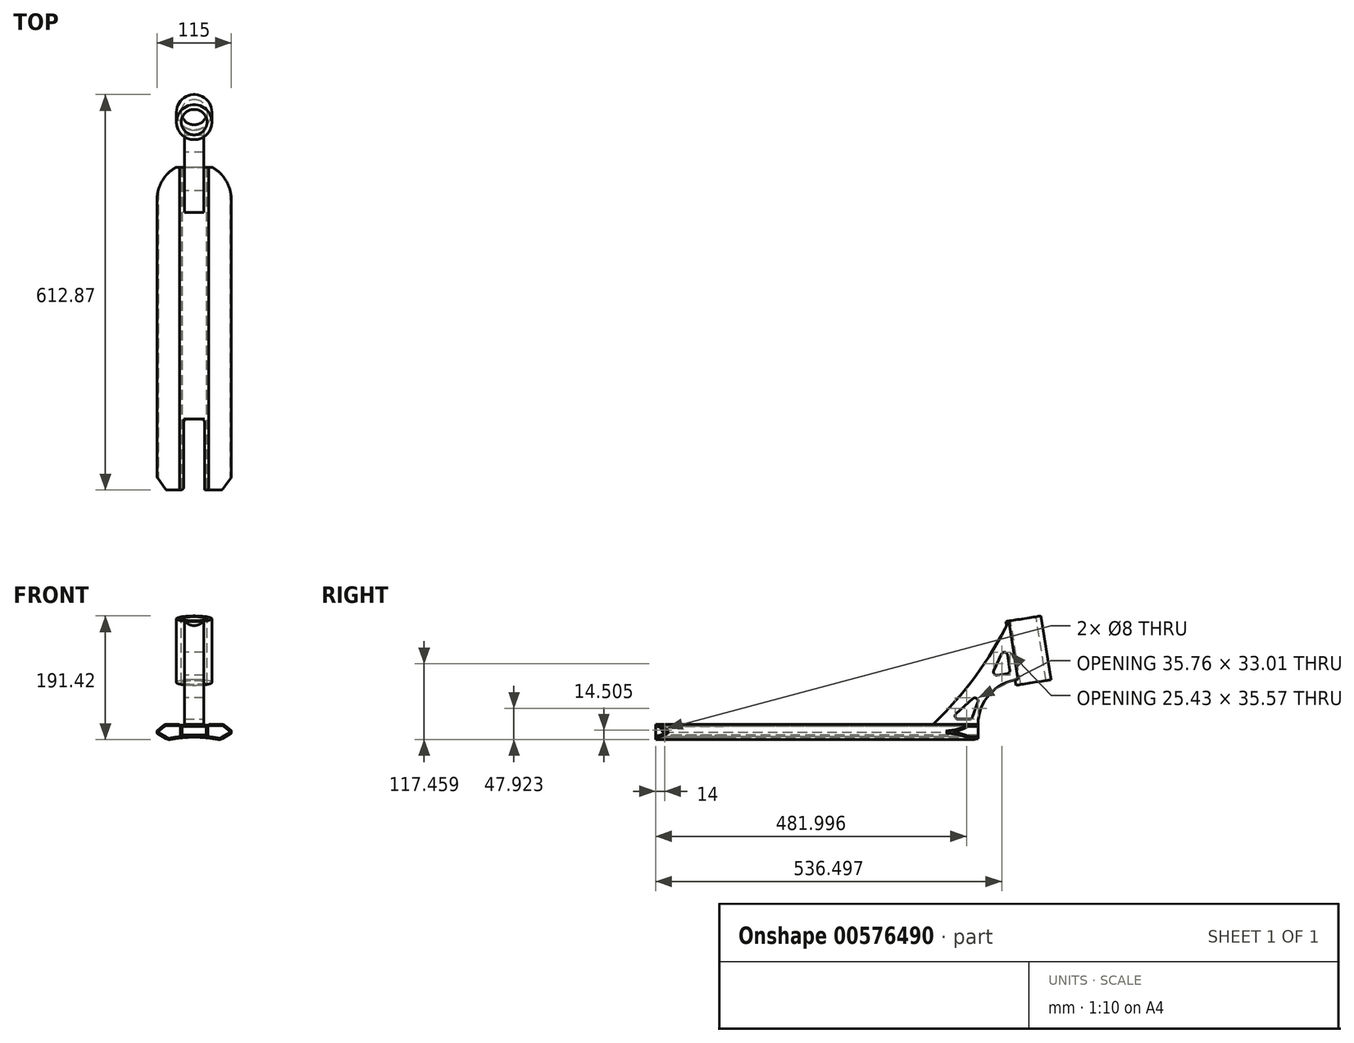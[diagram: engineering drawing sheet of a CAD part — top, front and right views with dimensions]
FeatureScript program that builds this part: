
annotation { "Feature Type Name" : "Feature", "Feature Type Description" : "" }
export const myFeature = defineFeature(function(context is Context, id is Id, definition is map)
    precondition{}
    {
        {
            var Q0;
            Q0=qCreatedBy(makeId("Front.planeOp"),FACE);
            var sketch = newSketch(context, id + "F0", { "sketchPlane" : qUnion([Q0])});
            skLineSegment(sketch, "E0", {"start": v(0, 18.62) * mm, "end": v(22.5, 18.62) * mm});
            skLineSegment(sketch, "E1", {"start": v(22.5, 18.62) * mm, "end": v(22.5, 19.92) * mm});
            skLineSegment(sketch, "E2", {"start": v(22.5, 19.92) * mm, "end": v(45.58, 19.92) * mm});
            skLineSegment(sketch, "E3", {"start": v(45.58, 19.92) * mm, "end": v(57.5, 9.92) * mm});
            skLineSegment(sketch, "E4", {"start": v(57.5, 9.92) * mm, "end": v(57.5, 5.92) * mm});
            skLineSegment(sketch, "E5", {"start": v(57.5, 5.92) * mm, "end": v(40.18, -4.08) * mm});
            skLineSegment(sketch, "E6.MirrorCS", {"start": v(0, 18.62) * mm, "end": v(-22.5, 18.62) * mm});
            skLineSegment(sketch, "E7.MirrorCS", {"start": v(-22.5, 18.62) * mm, "end": v(-22.5, 19.92) * mm});
            skLineSegment(sketch, "E8.MirrorCS", {"start": v(-22.5, 19.92) * mm, "end": v(-45.58, 19.92) * mm});
            skLineSegment(sketch, "E9.MirrorCS", {"start": v(-45.58, 19.92) * mm, "end": v(-57.5, 9.92) * mm});
            skLineSegment(sketch, "E10.MirrorCS", {"start": v(-57.5, 9.92) * mm, "end": v(-57.5, 5.92) * mm});
            skLineSegment(sketch, "E11.MirrorCS", {"start": v(-57.5, 5.92) * mm, "end": v(-40.18, -4.08) * mm});
            skArc(sketch, "E12", {"start": v(40.18, -4.08) * mm, "mid": v(0, 0) * mm, "end": v(-40.18, -4.08) * mm});
            skSolve(sketch);
        }
        {
            var Q0;
            Q0=makeQuery(id+"F0.imprint","IMPRINT",FACE,{"disambiguationData":[TD([[makeQuery(id+"F0.imprint","IMPRINT",EDGE,{"derivedFrom":sQuery(id+"F0.wireOp",EDGE,"E0")}),-1.0]])]});
            extrude(context, id + "F1", {"entities" : qUnion([Q0]), "endBound" : BoundingType.SYMMETRIC, "depth" : 500 * mm, "offsetDistance" : 25 * mm});
        }
        {
            var Q0;
            Q0=qCreatedBy(makeId("Front.planeOp"),FACE);
            var sketch = newSketch(context, id + "F2", { "sketchPlane" : qUnion([Q0])});
            skLineSegment(sketch, "E13.bottom", {"start": v(-19, 16.62) * mm, "end": v(19, 16.62) * mm});
            skLineSegment(sketch, "E13.top", {"start": v(-19, 3.62) * mm, "end": v(19, 3.62) * mm});
            skLineSegment(sketch, "E13.left", {"start": v(-19, 16.62) * mm, "end": v(-19, 3.62) * mm});
            skLineSegment(sketch, "E13.right", {"start": v(19, 16.62) * mm, "end": v(19, 3.62) * mm});
            skSolve(sketch);
        }
        {
            var Q0;
            Q0 = qSketchRegion(id + "F2", true);
            extrude(context, id + "F3", {"entities" : qUnion([Q0]), "operationType" : NewBodyOperationType.REMOVE, "endBound" : BoundingType.SYMMETRIC, "oppositeDirection" : true, "depth" : 500 * mm, "offsetDistance" : 25 * mm});
        }
        {
            var Q0;
            Q0=makeQuery(id+"F1.opExtrude","SWEPT_EDGE",EDGE,{"disambiguationData":[OSD([sQuery(id+"F0.wireOp",EDGE,"E7.MirrorCS"),sQuery(id+"F0.wireOp",EDGE,"E8.MirrorCS")])]});
            var Q1;
            Q1=makeQuery(id+"F1.opExtrude","SWEPT_EDGE",EDGE,{"disambiguationData":[OSD([sQuery(id+"F0.wireOp",EDGE,"E1"),sQuery(id+"F0.wireOp",EDGE,"E2")])]});
            fillet(context, id + "F4", {"entities" : qUnion([Q0, Q1]), "radius" : 2 * mm, "tangentPropagation" : true, "allowEdgeOverflow" : false});
        }
        {
            var Q0;
            Q0=makeQuery(id+"F1.opExtrude","SWEPT_EDGE",EDGE,{"disambiguationData":[OSD([sQuery(id+"F0.wireOp",EDGE,"E2"),sQuery(id+"F0.wireOp",EDGE,"E3")])]});
            var Q1;
            Q1=makeQuery(id+"F1.opExtrude","SWEPT_EDGE",EDGE,{"disambiguationData":[OSD([sQuery(id+"F0.wireOp",EDGE,"E8.MirrorCS"),sQuery(id+"F0.wireOp",EDGE,"E9.MirrorCS")])]});
            var Q2;
            Q2=makeQuery(id+"F1.opExtrude","SWEPT_EDGE",EDGE,{"disambiguationData":[OSD([sQuery(id+"F0.wireOp",EDGE,"E5"),sQuery(id+"F0.wireOp",EDGE,"E12")])]});
            var Q3;
            Q3=makeQuery(id+"F1.opExtrude","SWEPT_EDGE",EDGE,{"disambiguationData":[OSD([sQuery(id+"F0.wireOp",EDGE,"E11.MirrorCS"),sQuery(id+"F0.wireOp",EDGE,"E12")])]});
            fillet(context, id + "F5", {"entities" : qUnion([Q0, Q1, Q2, Q3]), "radius" : 9 * mm, "tangentPropagation" : true, "allowEdgeOverflow" : false});
        }
        {
            var Q0;
            Q0=makeQuery(id+"F1.opExtrude","SWEPT_EDGE",EDGE,{"disambiguationData":[OSD([sQuery(id+"F0.wireOp",EDGE,"E3"),sQuery(id+"F0.wireOp",EDGE,"E4")])]});
            var Q1;
            Q1=makeQuery(id+"F1.opExtrude","SWEPT_EDGE",EDGE,{"disambiguationData":[OSD([sQuery(id+"F0.wireOp",EDGE,"E4"),sQuery(id+"F0.wireOp",EDGE,"E5")])]});
            var Q2;
            Q2=makeQuery(id+"F1.opExtrude","SWEPT_EDGE",EDGE,{"disambiguationData":[OSD([sQuery(id+"F0.wireOp",EDGE,"E9.MirrorCS"),sQuery(id+"F0.wireOp",EDGE,"E10.MirrorCS")])]});
            var Q3;
            Q3=makeQuery(id+"F1.opExtrude","SWEPT_EDGE",EDGE,{"disambiguationData":[OSD([sQuery(id+"F0.wireOp",EDGE,"E10.MirrorCS"),sQuery(id+"F0.wireOp",EDGE,"E11.MirrorCS")])]});
            fillet(context, id + "F6", {"entities" : qUnion([Q0, Q1, Q2, Q3]), "radius" : 1 * mm, "tangentPropagation" : true, "allowEdgeOverflow" : false});
        }
        {
            var Q0;
            Q0=makeQuery(id+"F1.opExtrude","CAP_FACE",FACE,{"disambiguationData":[OSD([sQuery(id+"F0.wireOp",EDGE,"E0"),sQuery(id+"F0.wireOp",EDGE,"E1"),sQuery(id+"F0.wireOp",EDGE,"E2"),sQuery(id+"F0.wireOp",EDGE,"E3"),sQuery(id+"F0.wireOp",EDGE,"E4"),sQuery(id+"F0.wireOp",EDGE,"E5"),sQuery(id+"F0.wireOp",EDGE,"E6.MirrorCS"),sQuery(id+"F0.wireOp",EDGE,"E7.MirrorCS"),sQuery(id+"F0.wireOp",EDGE,"E8.MirrorCS"),sQuery(id+"F0.wireOp",EDGE,"E9.MirrorCS"),sQuery(id+"F0.wireOp",EDGE,"E10.MirrorCS"),sQuery(id+"F0.wireOp",EDGE,"E11.MirrorCS"),sQuery(id+"F0.wireOp",EDGE,"E12")])],"isStart":false});
            var sketch = newSketch(context, id + "F7", { "sketchPlane" : qUnion([Q0])});
            skArc(sketch, "E14.0", {"start": v(-22.5, 18.62) * mm, "mid": v(-23.23, 19.57) * mm, "end": v(-24.37, 19.92) * mm});
            skLineSegment(sketch, "E15.0", {"start": v(-24.37, 19.92) * mm, "end": v(-42.3, 19.92) * mm});
            skArc(sketch, "E16.0", {"start": v(-42.3, 19.92) * mm, "mid": v(-45.38, 19.38) * mm, "end": v(-48.1, 17.82) * mm});
            skLineSegment(sketch, "E17.0", {"start": v(-48.1, 17.82) * mm, "end": v(-57.14, 10.22) * mm});
            skArc(sketch, "E18.0", {"start": v(-57.14, 10.22) * mm, "mid": v(-57.4, 9.88) * mm, "end": v(-57.5, 9.46) * mm});
            skLineSegment(sketch, "E19.0", {"start": v(-57.5, 9.46) * mm, "end": v(-57.5, 6.5) * mm});
            skArc(sketch, "E20.0", {"start": v(-57.5, 6.5) * mm, "mid": v(-57.37, 6) * mm, "end": v(-57, 5.63) * mm});
            skLineSegment(sketch, "E21.0", {"start": v(-57, 5.63) * mm, "end": v(-43.1, -2.4) * mm});
            skArc(sketch, "E22.0", {"start": v(-43.1, -2.4) * mm, "mid": v(-40.12, -3.47) * mm, "end": v(-36.94, -3.44) * mm});
            skArc(sketch, "E23.0", {"start": v(36.94, -3.44) * mm, "mid": v(0, 0) * mm, "end": v(-36.94, -3.44) * mm});
            skArc(sketch, "E24.0", {"start": v(-21, 0.9) * mm, "mid": v(-29.18, -0.12) * mm, "end": v(-37.3, -1.48) * mm});
            skArc(sketch, "E24.1", {"start": v(-42.1, -0.66) * mm, "mid": v(-39.78, -1.5) * mm, "end": v(-37.3, -1.48) * mm});
            skLineSegment(sketch, "E24.2", {"start": v(-55.5, 7.08) * mm, "end": v(-42.1, -0.66) * mm});
            skLineSegment(sketch, "E24.4", {"start": v(-24.37, 17.92) * mm, "end": v(-24.37, 17.92) * mm});
            skLineSegment(sketch, "E24.5", {"start": v(-24.37, 17.92) * mm, "end": v(-42.3, 17.92) * mm});
            skArc(sketch, "E24.6", {"start": v(-42.3, 17.92) * mm, "mid": v(-44.7, 17.5) * mm, "end": v(-46.8, 16.28) * mm});
            skLineSegment(sketch, "E24.7", {"start": v(-46.8, 16.28) * mm, "end": v(-55.76, 8.77) * mm});
            skLineSegment(sketch, "E25.0", {"start": v(-21, 16.62) * mm, "end": v(-21, 3.62) * mm});
            skLineSegment(sketch, "E26.0", {"start": v(-22.5, 16.62) * mm, "end": v(-21, 16.62) * mm});
            skArc(sketch, "E27", {"start": v(-22.5, 16.62) * mm, "mid": v(-23.23, 17.57) * mm, "end": v(-24.37, 17.92) * mm});
            skLineSegment(sketch, "E28", {"start": v(-21, 3.62) * mm, "end": v(-21, 0.9) * mm});
            skLineSegment(sketch, "E29.MirrorCS", {"start": v(21, 16.62) * mm, "end": v(21, 3.62) * mm});
            skLineSegment(sketch, "E30.MirrorCS", {"start": v(24.37, 17.92) * mm, "end": v(42.3, 17.92) * mm});
            skArc(sketch, "E31.MirrorCS", {"start": v(22.5, 16.62) * mm, "mid": v(23.23, 17.57) * mm, "end": v(24.37, 17.92) * mm});
            skLineSegment(sketch, "E32.MirrorCS", {"start": v(22.5, 16.62) * mm, "end": v(21, 16.62) * mm});
            skArc(sketch, "E33.MirrorCS", {"start": v(42.3, 17.92) * mm, "mid": v(44.7, 17.5) * mm, "end": v(46.8, 16.28) * mm});
            skLineSegment(sketch, "E34.MirrorCS", {"start": v(46.8, 16.28) * mm, "end": v(55.76, 8.77) * mm});
            skLineSegment(sketch, "E35.MirrorCS", {"start": v(55.5, 7.08) * mm, "end": v(42.1, -0.66) * mm});
            skArc(sketch, "E36", {"start": v(-55.76, 8.77) * mm, "mid": v(-56.1, 7.85) * mm, "end": v(-55.5, 7.08) * mm});
            skArc(sketch, "E37.MirrorCS", {"start": v(42.1, -0.66) * mm, "mid": v(39.78, -1.5) * mm, "end": v(37.3, -1.48) * mm});
            skArc(sketch, "E38.MirrorCS", {"start": v(21, 0.9) * mm, "mid": v(29.18, -0.12) * mm, "end": v(37.3, -1.48) * mm});
            skLineSegment(sketch, "E39.MirrorCS", {"start": v(21, 3.62) * mm, "end": v(21, 0.9) * mm});
            skArc(sketch, "E40", {"start": v(55.5, 7.08) * mm, "mid": v(56.1, 7.85) * mm, "end": v(55.76, 8.77) * mm});
            skSolve(sketch);
        }
        {
            var Q0;
            Q0=makeQuery(id+"F7.imprint","IMPRINT",FACE,{"disambiguationData":[TD([[makeQuery(id+"F7.imprint","IMPRINT",EDGE,{"derivedFrom":sQuery(id+"F7.wireOp",EDGE,"E29.MirrorCS")}),1.0]])]});
            var Q1;
            Q1=makeQuery(id+"F7.imprint","IMPRINT",FACE,{"disambiguationData":[TD([[makeQuery(id+"F7.imprint","IMPRINT",EDGE,{"derivedFrom":sQuery(id+"F7.wireOp",EDGE,"E24.0")}),-1.0]])]});
            extrude(context, id + "F8", {"entities" : qUnion([Q0, Q1]), "operationType" : NewBodyOperationType.REMOVE, "oppositeDirection" : true, "depth" : 500 * mm, "offsetDistance" : 25 * mm});
        }
        {
            var Q0;
            Q0=qCreatedBy(makeId("Top.planeOp"),FACE);
            var sketch = newSketch(context, id + "F9", { "sketchPlane" : qUnion([Q0])});
            skArc(sketch, "E41", {"start": v(57.5, 200) * mm, "mid": v(-0.3, 257.5) * mm, "end": v(-57.5, 199.42) * mm});
            skLineSegment(sketch, "E42", {"start": v(-57.5, 199.42) * mm, "end": v(-57.5, 280) * mm});
            skLineSegment(sketch, "E43", {"start": v(57.5, 200) * mm, "end": v(57.5, 280) * mm});
            skLineSegment(sketch, "E44", {"start": v(57.5, 280) * mm, "end": v(-57.5, 280) * mm});
            skSolve(sketch);
        }
        {
            var Q0;
            {var subQ0=sQuery(id+"F9.wireOp",EDGE,"E43");Q0=makeQuery(id+"F9.imprint","IMPRINT",FACE,{"disambiguationData":[TD([[makeQuery(id+"F9.imprint","IMPRINT",EDGE,{"derivedFrom":subQ0}),1.0]])]});}
            extrude(context, id + "F10", {"entities" : qUnion([Q0]), "operationType" : NewBodyOperationType.REMOVE, "endBound" : BoundingType.THROUGH_ALL, "oppositeDirection" : true, "depth" : 25 * mm, "offsetDistance" : 25 * mm, "hasSecondDirection" : true, "secondDirectionBound" : SecondDirectionBoundingType.THROUGH_ALL, "secondDirectionOppositeDirection" : false, "secondDirectionDepth" : 25 * mm});
        }
        {
            var Q0;
            Q0=qCreatedBy(makeId("Top.planeOp"),FACE);
            var sketch = newSketch(context, id + "F11", { "sketchPlane" : qUnion([Q0])});
            skLineSegment(sketch, "E45", {"start": v(-43.3, -250) * mm, "end": v(-16, -250) * mm});
            skLineSegment(sketch, "E46", {"start": v(-16, -250) * mm, "end": v(-16, -140) * mm});
            skLineSegment(sketch, "E47", {"start": v(-16, -140) * mm, "end": v(16, -140) * mm});
            skLineSegment(sketch, "E48", {"start": v(16, -140) * mm, "end": v(16, -250) * mm});
            skLineSegment(sketch, "E49", {"start": v(16, -250) * mm, "end": v(43.3, -250) * mm});
            skLineSegment(sketch, "E50", {"start": v(43.3, -250) * mm, "end": v(68, -216) * mm});
            skLineSegment(sketch, "E51", {"start": v(68, -216) * mm, "end": v(68, -346) * mm});
            skLineSegment(sketch, "E52", {"start": v(68, -346) * mm, "end": v(-68, -346) * mm});
            skLineSegment(sketch, "E53", {"start": v(-68, -346) * mm, "end": v(-68, -216) * mm});
            skLineSegment(sketch, "E54", {"start": v(-68, -216) * mm, "end": v(-43.3, -250) * mm});
            skSolve(sketch);
        }
        {
            var Q0;
            Q0 = qSketchRegion(id + "F11", true);
            var Q1;
            Q1=makeQuery(id+"F11.imprint","IMPRINT",FACE,{"disambiguationData":[TD([[makeQuery(id+"F11.imprint","IMPRINT",EDGE,{"derivedFrom":sQuery(id+"F11.wireOp",EDGE,"E45")}),-1.0]])]});
            extrude(context, id + "F12", {"entities" : qUnion([Q0, Q1]), "operationType" : NewBodyOperationType.REMOVE, "endBound" : BoundingType.THROUGH_ALL, "oppositeDirection" : true, "depth" : 25 * mm, "offsetDistance" : 25 * mm, "hasSecondDirection" : true, "secondDirectionBound" : SecondDirectionBoundingType.THROUGH_ALL, "secondDirectionOppositeDirection" : false, "secondDirectionDepth" : 25 * mm});
        }
        {
            var Q0;
            {var subQ0=sQuery(id+"F11.wireOp",EDGE,"E47");var subQ1=sQuery(id+"F11.wireOp",EDGE,"E46");Q0=makeQuery(id+"F12.boolean.opBoolean","COPY",EDGE,{"disambiguationData":[TD([makeQuery(id+"F3.boolean.opBoolean","COPY",FACE,{"derivedFrom":makeQuery(id+"F3.opExtrude","SWEPT_FACE",FACE,{"disambiguationData":[OSD([sQuery(id+"F2.wireOp",EDGE,"E13.bottom")])]})})])],"derivedFrom":makeQuery(id+"F12.opExtrude","SWEPT_EDGE",EDGE,{"disambiguationData":[OSD([subQ1,subQ0])]})});}
            var Q1;
            {var subQ2=sQuery(id+"F11.wireOp",EDGE,"E46");Q1=makeQuery(id+"F12.boolean.opBoolean","COPY",EDGE,{"disambiguationData":[TD([makeQuery(id+"F3.boolean.opBoolean","COPY",FACE,{"derivedFrom":makeQuery(id+"F3.opExtrude","SWEPT_FACE",FACE,{"disambiguationData":[OSD([sQuery(id+"F2.wireOp",EDGE,"E13.bottom")])]})})])],"derivedFrom":makeQuery(id+"F12.opExtrude","SWEPT_EDGE",EDGE,{"disambiguationData":[OSD([sQuery(id+"F11.wireOp",EDGE,"E45"),subQ2])]})});}
            var Q2;
            {var subQ0=sQuery(id+"F11.wireOp",EDGE,"E47");var subQ1=sQuery(id+"F11.wireOp",EDGE,"E48");Q2=makeQuery(id+"F12.boolean.opBoolean","COPY",EDGE,{"disambiguationData":[TD([makeQuery(id+"F3.boolean.opBoolean","COPY",FACE,{"derivedFrom":makeQuery(id+"F3.opExtrude","SWEPT_FACE",FACE,{"disambiguationData":[OSD([sQuery(id+"F2.wireOp",EDGE,"E13.bottom")])]})})])],"derivedFrom":makeQuery(id+"F12.opExtrude","SWEPT_EDGE",EDGE,{"disambiguationData":[OSD([subQ0,subQ1])]})});}
            var Q3;
            {var subQ2=sQuery(id+"F11.wireOp",EDGE,"E48");Q3=makeQuery(id+"F12.boolean.opBoolean","COPY",EDGE,{"disambiguationData":[TD([makeQuery(id+"F3.boolean.opBoolean","COPY",FACE,{"derivedFrom":makeQuery(id+"F3.opExtrude","SWEPT_FACE",FACE,{"disambiguationData":[OSD([sQuery(id+"F2.wireOp",EDGE,"E13.bottom")])]})})])],"derivedFrom":makeQuery(id+"F12.opExtrude","SWEPT_EDGE",EDGE,{"disambiguationData":[OSD([subQ2,sQuery(id+"F11.wireOp",EDGE,"E49")])]})});}
            fillet(context, id + "F13", {"entities" : qUnion([Q0, Q1, Q2, Q3]), "radius" : 5 * mm, "tangentPropagation" : true, "allowEdgeOverflow" : false});
        }
        {
            var Q0;
            Q0=qCreatedBy(makeId("Right.planeOp"),FACE);
            var sketch = newSketch(context, id + "F14", { "sketchPlane" : qUnion([Q0])});
            skLineSegment(sketch, "E55", {"start": v(250, 19.92) * mm, "end": v(180, 19.92) * mm});
            skArc(sketch, "E56", {"start": v(180, 19.92) * mm, "mid": v(245.95, 94.59) * mm, "end": v(297.35, 179.92) * mm});
            skLineSegment(sketch, "E57", {"start": v(297.35, 179.92) * mm, "end": v(342.78, 187.12) * mm});
            skLineSegment(sketch, "E58", {"start": v(342.78, 187.12) * mm, "end": v(358.42, 88.35) * mm});
            skLineSegment(sketch, "E59", {"start": v(358.42, 88.35) * mm, "end": v(313, 81.15) * mm});
            skLineSegment(sketch, "E60", {"start": v(313, 81.15) * mm, "end": v(311.68, 89.43) * mm});
            skArc(sketch, "E61", {"start": v(311.68, 89.43) * mm, "mid": v(267.64, 66.39) * mm, "end": v(250, 19.92) * mm});
            skSolve(sketch);
        }
        {
            var Q0;
            Q0 = qSketchRegion(id + "F14", true);
            extrude(context, id + "F15", {"entities" : qUnion([Q0]), "operationType" : NewBodyOperationType.ADD, "endBound" : BoundingType.SYMMETRIC, "depth" : 30 * mm, "offsetDistance" : 25 * mm});
        }
        {
            var Q0;
            Q0=makeQuery(id+"F15.opExtrude","SWEPT_FACE",FACE,{"disambiguationData":[OSD([sQuery(id+"F14.wireOp",EDGE,"E57")])]});
            var sketch = newSketch(context, id + "F16", { "sketchPlane" : qUnion([Q0])});
            skCircle(sketch, "E62", {"center": v(0, 344.83) * mm, "radius": 27.5 * mm});
            skSolve(sketch);
        }
        {
            var Q0;
            Q0=makeQuery(id+"F16.imprint","IMPRINT",FACE,{"disambiguationData":[TD([[makeQuery(id+"F16.imprint","IMPRINT",EDGE,{"derivedFrom":sQuery(id+"F16.wireOp",EDGE,"E62")}),1.0]])]});
            extrude(context, id + "F17", {"entities" : qUnion([Q0]), "operationType" : NewBodyOperationType.ADD, "oppositeDirection" : true, "depth" : 100 * mm, "offsetDistance" : 25 * mm});
        }
        {
            var Q0;
            {var subQ0=sQuery(id+"F14.wireOp",EDGE,"E57");Q0=makeQuery(id+"F17.boolean.opBoolean","MERGE",FACE,{"derivedFrom":[makeQuery(id+"F15.opExtrude","SWEPT_FACE",FACE,{"disambiguationData":[OSD([subQ0])]}),makeQuery(id+"F17.opExtrude","CAP_FACE",FACE,{"disambiguationData":[OSD([sQuery(id+"F14.wireOp",EDGE,"E56"),subQ0,sQuery(id+"F14.wireOp",EDGE,"E58"),sQuery(id+"F16.wireOp",EDGE,"E62")])],"isStart":true})]});}
            var sketch = newSketch(context, id + "F18", { "sketchPlane" : qUnion([Q0])});
            skPoint(sketch, "E63", {"position": v(0, 344.83) * mm});
            skSolve(sketch);
        }
        {
            var Q0;
            Q0=sQuery(id+"F18.wireOp",VERTEX,"E63");
            var Q1;
            Q1=makeQuery(id+"F15.opExtrude","SWEPT_BODY",BODY,{"disambiguationData":[OSD([sQuery(id+"F14.wireOp",EDGE,"E55"),sQuery(id+"F14.wireOp",EDGE,"E56"),sQuery(id+"F14.wireOp",EDGE,"E57"),sQuery(id+"F14.wireOp",EDGE,"E58"),sQuery(id+"F14.wireOp",EDGE,"E59"),sQuery(id+"F14.wireOp",EDGE,"E60"),sQuery(id+"F14.wireOp",EDGE,"E61")])]});
            hole(context, id + "F19", {"style" : HoleStyle.SIMPLE, "endStyle" : HoleEndStyle.THROUGH, "holeDiameter" : 40 * mm, "majorDiameter" : 5 * mm, "isTappedThrough" : true, "tappedDepth" : 12 * mm, "tapClearance" : 3, "locations" : qUnion([Q0]), "scope" : qUnion([Q1])});
        }
        {
            var Q0;
            Q0=makeQuery(id+"F8.boolean.opBoolean","COPY",FACE,{"derivedFrom":makeQuery(id+"F8.opExtrude","SWEPT_FACE",FACE,{"disambiguationData":[OSD([sQuery(id+"F7.wireOp",EDGE,"E29.MirrorCS"),sQuery(id+"F7.wireOp",EDGE,"E39.MirrorCS")])]})});
            var sketch = newSketch(context, id + "F20", { "sketchPlane" : qUnion([Q0])});
            skPoint(sketch, "E64", {"position": v(-236, 10.9) * mm});
            skPoint(sketch, "E64.positionSnap0", {"position": v(-250, 10.9) * mm});
            skSolve(sketch);
        }
        {
            var Q0;
            Q0=sQuery(id+"F20.wireOp",VERTEX,"E64");
            var Q1;
            Q1=makeQuery(id+"F1.opExtrude","SWEPT_BODY",BODY,{"disambiguationData":[OSD([sQuery(id+"F0.wireOp",EDGE,"E0"),sQuery(id+"F0.wireOp",EDGE,"E1"),sQuery(id+"F0.wireOp",EDGE,"E2"),sQuery(id+"F0.wireOp",EDGE,"E3"),sQuery(id+"F0.wireOp",EDGE,"E4"),sQuery(id+"F0.wireOp",EDGE,"E5"),sQuery(id+"F0.wireOp",EDGE,"E6.MirrorCS"),sQuery(id+"F0.wireOp",EDGE,"E7.MirrorCS"),sQuery(id+"F0.wireOp",EDGE,"E8.MirrorCS"),sQuery(id+"F0.wireOp",EDGE,"E9.MirrorCS"),sQuery(id+"F0.wireOp",EDGE,"E10.MirrorCS"),sQuery(id+"F0.wireOp",EDGE,"E11.MirrorCS"),sQuery(id+"F0.wireOp",EDGE,"E12")])]});
            hole(context, id + "F21", {"style" : HoleStyle.SIMPLE, "endStyle" : HoleEndStyle.BLIND, "holeDiameter" : 8 * mm, "majorDiameter" : 5 * mm, "holeDepth" : 42.5 * mm, "isTappedThrough" : true, "tappedDepth" : 12 * mm, "tapClearance" : 3, "locations" : qUnion([Q0]), "scope" : qUnion([Q1])});
        }
        {
            var Q0;
            Q0=makeQuery(id+"F15.opExtrude","CAP_FACE",FACE,{"disambiguationData":[OSD([sQuery(id+"F14.wireOp",EDGE,"E55"),sQuery(id+"F14.wireOp",EDGE,"E56"),sQuery(id+"F14.wireOp",EDGE,"E57"),sQuery(id+"F14.wireOp",EDGE,"E58"),sQuery(id+"F14.wireOp",EDGE,"E59"),sQuery(id+"F14.wireOp",EDGE,"E60"),sQuery(id+"F14.wireOp",EDGE,"E61")])],"isStart":false});
            var sketch = newSketch(context, id + "F22", { "sketchPlane" : qUnion([Q0])});
            skLineSegment(sketch, "E65", {"start": v(292.9, 143.78) * mm, "end": v(299.94, 99.34) * mm});
            skLineSegment(sketch, "E66", {"start": v(299.94, 99.34) * mm, "end": v(270.3, 94.64) * mm});
            skLineSegment(sketch, "E67", {"start": v(270.3, 94.64) * mm, "end": v(292.9, 143.78) * mm});
            skLineSegment(sketch, "E68", {"start": v(206, 27.82) * mm, "end": v(240, 27.82) * mm});
            skLineSegment(sketch, "E69", {"start": v(240, 27.82) * mm, "end": v(256.38, 72.82) * mm});
            skLineSegment(sketch, "E70", {"start": v(256.38, 72.82) * mm, "end": v(206, 27.82) * mm});
            skSolve(sketch);
        }
        {
            var Q0;
            Q0=makeQuery(id+"F22.imprint","IMPRINT",FACE,{"disambiguationData":[TD([[makeQuery(id+"F22.imprint","IMPRINT",EDGE,{"derivedFrom":sQuery(id+"F22.wireOp",EDGE,"E68")}),1.0]])]});
            var Q1;
            Q1=makeQuery(id+"F22.imprint","IMPRINT",FACE,{"disambiguationData":[TD([[makeQuery(id+"F22.imprint","IMPRINT",EDGE,{"derivedFrom":sQuery(id+"F22.wireOp",EDGE,"E65")}),-1.0]])]});
            extrude(context, id + "F23", {"entities" : qUnion([Q0, Q1]), "operationType" : NewBodyOperationType.REMOVE, "endBound" : BoundingType.THROUGH_ALL, "oppositeDirection" : true, "depth" : 25 * mm, "offsetDistance" : 25 * mm});
        }
        {
            var Q0;
            Q0=makeQuery(id+"F23.boolean.opBoolean","COPY",EDGE,{"derivedFrom":makeQuery(id+"F23.opExtrude","SWEPT_EDGE",EDGE,{"disambiguationData":[OSD([sQuery(id+"F22.wireOp",EDGE,"E68"),sQuery(id+"F22.wireOp",EDGE,"E70")])]})});
            var Q1;
            Q1=makeQuery(id+"F23.boolean.opBoolean","COPY",EDGE,{"derivedFrom":makeQuery(id+"F23.opExtrude","SWEPT_EDGE",EDGE,{"disambiguationData":[OSD([sQuery(id+"F22.wireOp",EDGE,"E69"),sQuery(id+"F22.wireOp",EDGE,"E70")])]})});
            var Q2;
            Q2=makeQuery(id+"F23.boolean.opBoolean","COPY",EDGE,{"derivedFrom":makeQuery(id+"F23.opExtrude","SWEPT_EDGE",EDGE,{"disambiguationData":[OSD([sQuery(id+"F22.wireOp",EDGE,"E68"),sQuery(id+"F22.wireOp",EDGE,"E69")])]})});
            var Q3;
            Q3=makeQuery(id+"F23.boolean.opBoolean","COPY",EDGE,{"derivedFrom":makeQuery(id+"F23.opExtrude","SWEPT_EDGE",EDGE,{"disambiguationData":[OSD([sQuery(id+"F22.wireOp",EDGE,"E65"),sQuery(id+"F22.wireOp",EDGE,"E66")])]})});
            var Q4;
            Q4=makeQuery(id+"F23.boolean.opBoolean","COPY",EDGE,{"derivedFrom":makeQuery(id+"F23.opExtrude","SWEPT_EDGE",EDGE,{"disambiguationData":[OSD([sQuery(id+"F22.wireOp",EDGE,"E66"),sQuery(id+"F22.wireOp",EDGE,"E67")])]})});
            var Q5;
            Q5=makeQuery(id+"F23.boolean.opBoolean","COPY",EDGE,{"derivedFrom":makeQuery(id+"F23.opExtrude","SWEPT_EDGE",EDGE,{"disambiguationData":[OSD([sQuery(id+"F22.wireOp",EDGE,"E65"),sQuery(id+"F22.wireOp",EDGE,"E67")])]})});
            fillet(context, id + "F24", {"entities" : qUnion([Q0, Q1, Q2, Q3, Q4, Q5]), "radius" : 5 * mm, "tangentPropagation" : true, "allowEdgeOverflow" : false});
        }
    });
